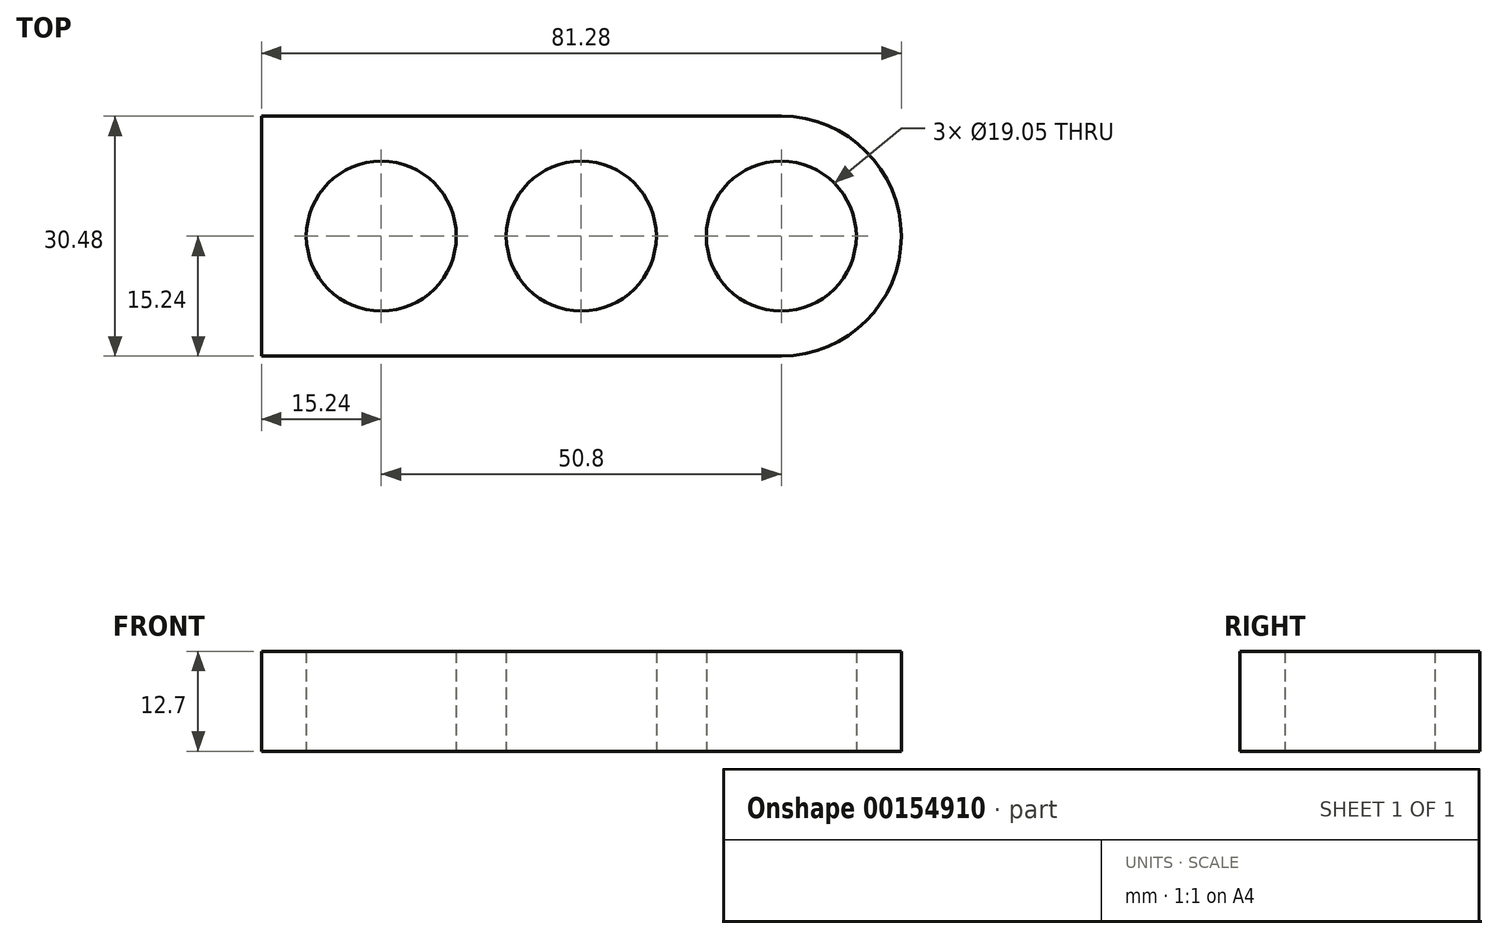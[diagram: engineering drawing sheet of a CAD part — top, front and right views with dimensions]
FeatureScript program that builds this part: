
annotation { "Feature Type Name" : "Feature", "Feature Type Description" : "" }
export const myFeature = defineFeature(function(context is Context, id is Id, definition is map)
    precondition{}
    {
        {
            var Q0;
            Q0=qCreatedBy(makeId("Top.planeOp"),FACE);
            var sketch = newSketch(context, id + "F0", { "sketchPlane" : qUnion([Q0])});
            skLineSegment(sketch, "E0.bottom", {"start": v(0, 0) * mm, "end": v(-81.28, 0) * mm});
            skLineSegment(sketch, "E0.top", {"start": v(0, 30.48) * mm, "end": v(-81.28, 30.48) * mm});
            skLineSegment(sketch, "E0.left", {"start": v(0, 0) * mm, "end": v(0, 30.48) * mm});
            skLineSegment(sketch, "E0.right", {"start": v(-81.28, 0) * mm, "end": v(-81.28, 30.48) * mm});
            skCircle(sketch, "E1", {"center": v(-15.24, 15.24) * mm, "radius": 9.53 * mm});
            skCircle(sketch, "E2.1.0.0", {"center": v(-40.64, 15.24) * mm, "radius": 9.53 * mm});
            skCircle(sketch, "E2.2.0.0", {"center": v(-66.04, 15.24) * mm, "radius": 9.53 * mm});
            skLineSegment(sketch, "E2.direction1", {"start": v(-15.24, 15.24) * mm, "end": v(-40.64, 15.24) * mm, "construction": true});
            skLineSegment(sketch, "E3", {"start": v(-15.24, 15.24) * mm, "end": v(-15.24, 0) * mm});
            skSolve(sketch);
        }
        {
            var Q0;
            Q0=makeQuery(id+"F0.imprint","IMPRINT",FACE,{"disambiguationData":[TD([[makeQuery(id+"F0.imprint","IMPRINT",EDGE,{"derivedFrom":sQuery(id+"F0.wireOp",EDGE,"E0.bottom")}),-1.0]])]});
            extrude(context, id + "F1", {"entities" : qUnion([Q0]), "depth" : 12.7 * mm});
        }
        {
            var Q0;
            Q0=makeQuery(id+"F1.opExtrude","SWEPT_EDGE",EDGE,{"disambiguationData":[OSD([sQuery(id+"F0.wireOp",EDGE,"E0.bottom"),sQuery(id+"F0.wireOp",EDGE,"E0.left")])]});
            var Q1;
            Q1=makeQuery(id+"F1.opExtrude","SWEPT_EDGE",EDGE,{"disambiguationData":[OSD([sQuery(id+"F0.wireOp",EDGE,"E0.top"),sQuery(id+"F0.wireOp",EDGE,"E0.left")])]});
            fillet(context, id + "F2", {"entities" : qUnion([Q0, Q1]), "radius" : 15.24 * mm, "tangentPropagation" : true, "allowEdgeOverflow" : false});
        }
    });
